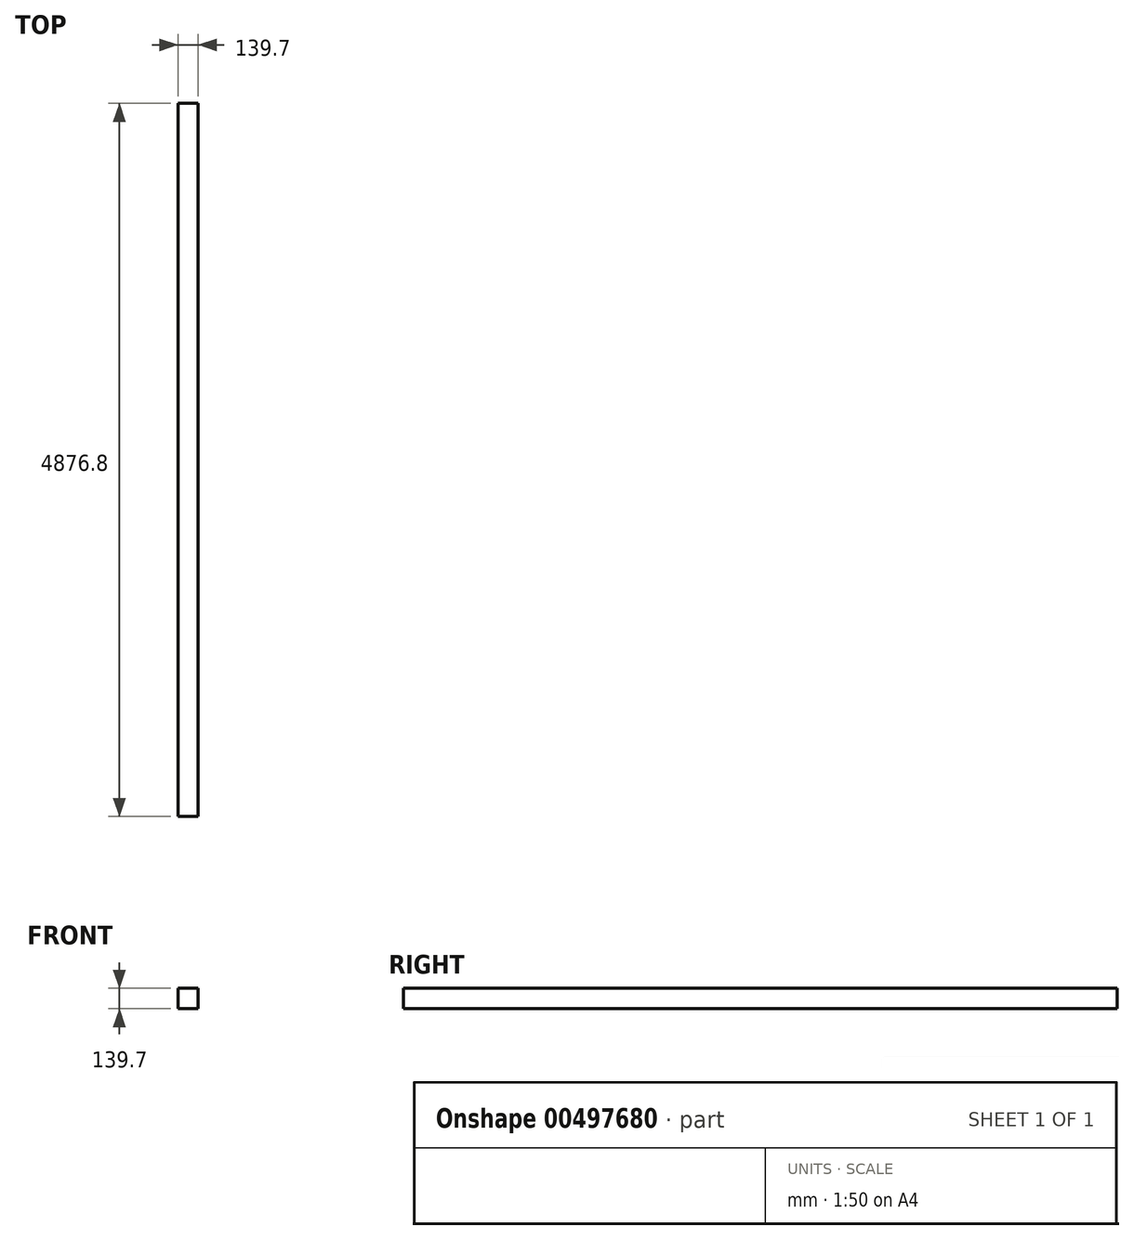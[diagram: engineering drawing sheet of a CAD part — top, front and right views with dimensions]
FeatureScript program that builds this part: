
annotation { "Feature Type Name" : "Feature", "Feature Type Description" : "" }
export const myFeature = defineFeature(function(context is Context, id is Id, definition is map)
    precondition{}
    {
        {
            var Q0;
            Q0=qCreatedBy(makeId("Front.planeOp"),FACE);
            var sketch = newSketch(context, id + "F0", { "sketchPlane" : qUnion([Q0])});
            skLineSegment(sketch, "E0.bottom", {"start": v(0, 0) * mm, "end": v(139.7, 0) * mm});
            skLineSegment(sketch, "E0.top", {"start": v(0, 139.7) * mm, "end": v(139.7, 139.7) * mm});
            skLineSegment(sketch, "E0.left", {"start": v(0, 0) * mm, "end": v(0, 139.7) * mm});
            skLineSegment(sketch, "E0.right", {"start": v(139.7, 0) * mm, "end": v(139.7, 139.7) * mm});
            skSolve(sketch);
        }
        {
            var Q0;
            Q0 = qSketchRegion(id + "F0", true);
            extrude(context, id + "F1", {"entities" : qUnion([Q0]), "depth" : 4876.8 * mm});
        }
    });
